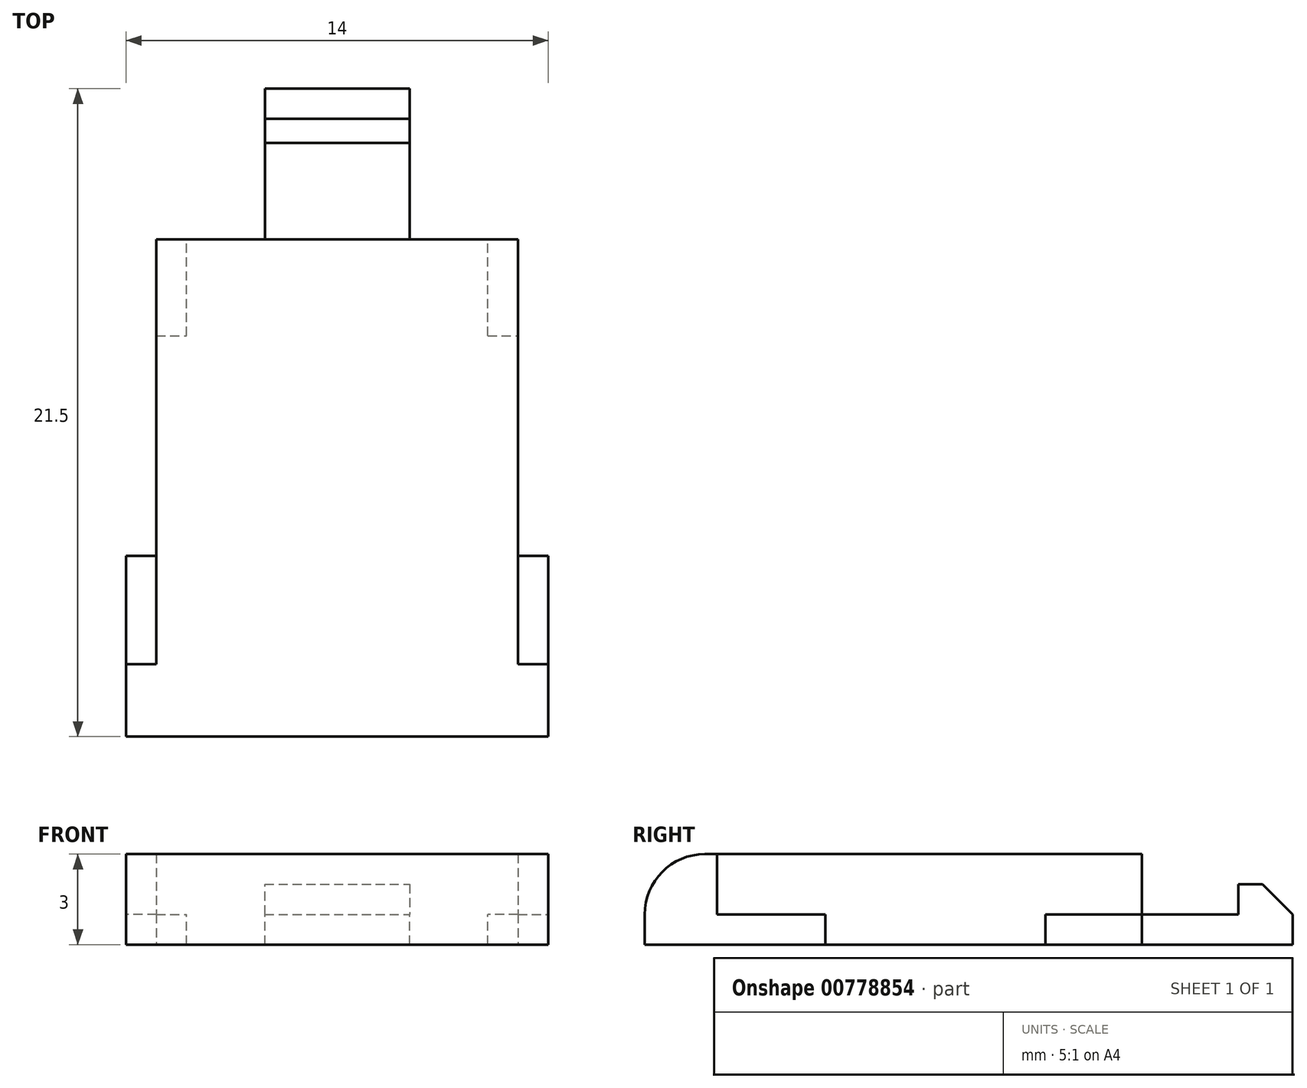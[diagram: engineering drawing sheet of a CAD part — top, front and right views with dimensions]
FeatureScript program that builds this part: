
annotation { "Feature Type Name" : "Feature", "Feature Type Description" : "" }
export const myFeature = defineFeature(function(context is Context, id is Id, definition is map)
    precondition{}
    {
        {
            var Q0;
            Q0=qCreatedBy(makeId("Front.planeOp"),FACE);
            var sketch = newSketch(context, id + "F0", { "sketchPlane" : qUnion([Q0])});
            skLineSegment(sketch, "E0.bottom", {"start": v(-6, 3) * mm, "end": v(6, 3) * mm});
            skLineSegment(sketch, "E0.top", {"start": v(-6, 0) * mm, "end": v(6, 0) * mm});
            skLineSegment(sketch, "E0.left", {"start": v(-6, 3) * mm, "end": v(-6, 0) * mm});
            skLineSegment(sketch, "E0.right", {"start": v(6, 3) * mm, "end": v(6, 0) * mm});
            skLineSegment(sketch, "E1", {"start": v(6, 1) * mm, "end": v(-6, 1) * mm});
            skLineSegment(sketch, "E2.bottom", {"start": v(6, 3) * mm, "end": v(7, 3) * mm});
            skLineSegment(sketch, "E2.top", {"start": v(6, 0) * mm, "end": v(7, 0) * mm});
            skLineSegment(sketch, "E2.right", {"start": v(7, 3) * mm, "end": v(7, 0) * mm});
            skLineSegment(sketch, "E3.bottom", {"start": v(-6, 3) * mm, "end": v(-7, 3) * mm});
            skLineSegment(sketch, "E3.top", {"start": v(-6, 0) * mm, "end": v(-7, 0) * mm});
            skLineSegment(sketch, "E3.right", {"start": v(-7, 3) * mm, "end": v(-7, 0) * mm});
            skLineSegment(sketch, "E4", {"start": v(-6, 1) * mm, "end": v(-7, 1) * mm});
            skLineSegment(sketch, "E5", {"start": v(6, 1) * mm, "end": v(7, 1) * mm});
            skPoint(sketch, "E6", {"position": v(0, 0) * mm});
            skSolve(sketch);
        }
        {
            var Q0;
            {var subQ0=sQuery(id+"F0.wireOp",EDGE,"E0.top");Q0=makeQuery(id+"F0.imprint","IMPRINT",FACE,{"disambiguationData":[TD([[makeQuery(id+"F0.imprint","IMPRINT",EDGE,{"derivedFrom":subQ0}),1.0]])]});}
            var Q1;
            {var subQ0=sQuery(id+"F0.wireOp",EDGE,"E0.bottom");Q1=makeQuery(id+"F0.imprint","IMPRINT",FACE,{"disambiguationData":[TD([[makeQuery(id+"F0.imprint","IMPRINT",EDGE,{"derivedFrom":subQ0}),-1.0]])]});}
            extrude(context, id + "F1", {"entities" : qUnion([Q0, Q1]), "oppositeDirection" : true, "depth" : 16.5 * mm, "offsetDistance" : 25 * mm});
        }
        {
            var Q0;
            {var subQ0=sQuery(id+"F0.wireOp",EDGE,"E3.bottom");Q0=makeQuery(id+"F0.imprint","IMPRINT",FACE,{"disambiguationData":[TD([[makeQuery(id+"F0.imprint","IMPRINT",EDGE,{"derivedFrom":subQ0}),1.0]])]});}
            var Q1;
            {var subQ0=sQuery(id+"F0.wireOp",EDGE,"E2.bottom");Q1=makeQuery(id+"F0.imprint","IMPRINT",FACE,{"disambiguationData":[TD([[makeQuery(id+"F0.imprint","IMPRINT",EDGE,{"derivedFrom":subQ0}),-1.0]])]});}
            extrude(context, id + "F2", {"entities" : qUnion([Q0, Q1]), "operationType" : NewBodyOperationType.ADD, "oppositeDirection" : true, "depth" : 2.4 * mm, "offsetDistance" : 25 * mm});
        }
        {
            var Q0;
            {var subQ0=sQuery(id+"F0.wireOp",EDGE,"E2.top");Q0=makeQuery(id+"F0.imprint","IMPRINT",FACE,{"disambiguationData":[TD([[makeQuery(id+"F0.imprint","IMPRINT",EDGE,{"derivedFrom":subQ0}),1.0]])]});}
            var Q1;
            {var subQ0=sQuery(id+"F0.wireOp",EDGE,"E3.top");Q1=makeQuery(id+"F0.imprint","IMPRINT",FACE,{"disambiguationData":[TD([[makeQuery(id+"F0.imprint","IMPRINT",EDGE,{"derivedFrom":subQ0}),-1.0]])]});}
            extrude(context, id + "F3", {"entities" : qUnion([Q0, Q1]), "operationType" : NewBodyOperationType.ADD, "oppositeDirection" : true, "depth" : 6 * mm, "offsetDistance" : 25 * mm});
        }
        {
            var Q0;
            Q0=makeQuery(id+"F2.boolean.opBoolean","MERGE",EDGE,{"derivedFrom":[makeQuery(id+"F1.opExtrude","CAP_EDGE",EDGE,{"disambiguationData":[OSD([sQuery(id+"F0.wireOp",EDGE,"E0.bottom")])],"isStart":true}),makeQuery(id+"F2.opExtrude","CAP_EDGE",EDGE,{"disambiguationData":[OSD([sQuery(id+"F0.wireOp",EDGE,"E2.bottom")])],"isStart":true}),makeQuery(id+"F2.opExtrude","CAP_EDGE",EDGE,{"disambiguationData":[OSD([sQuery(id+"F0.wireOp",EDGE,"E3.bottom")])],"isStart":true})]});
            fillet(context, id + "F4", {"entities" : qUnion([Q0]), "radius" : 2 * mm, "tangentPropagation" : true, "allowEdgeOverflow" : false});
        }
        {
            var Q0;
            Q0=makeQuery(id+"F1.opExtrude","CAP_FACE",FACE,{"disambiguationData":[OSD([sQuery(id+"F0.wireOp",EDGE,"E0.bottom"),sQuery(id+"F0.wireOp",EDGE,"E0.top"),sQuery(id+"F0.wireOp",EDGE,"E0.right"),sQuery(id+"F0.wireOp",EDGE,"E0.left")])],"isStart":false});
            var sketch = newSketch(context, id + "F5", { "sketchPlane" : qUnion([Q0])});
            skLineSegment(sketch, "E7.bottom", {"start": v(-6, 0) * mm, "end": v(-5, 0) * mm});
            skLineSegment(sketch, "E7.top", {"start": v(-6, 1) * mm, "end": v(-5, 1) * mm});
            skLineSegment(sketch, "E7.left", {"start": v(-6, 0) * mm, "end": v(-6, 1) * mm});
            skLineSegment(sketch, "E7.right", {"start": v(-5, 0) * mm, "end": v(-5, 1) * mm});
            skLineSegment(sketch, "E8.MirrorCS", {"start": v(6, 1) * mm, "end": v(5, 1) * mm});
            skLineSegment(sketch, "E9.MirrorCS", {"start": v(5, 0) * mm, "end": v(5, 1) * mm});
            skLineSegment(sketch, "E10.bottom", {"start": v(2.4, 0) * mm, "end": v(-2.4, 0) * mm});
            skLineSegment(sketch, "E10.top", {"start": v(2.4, 1) * mm, "end": v(-2.4, 1) * mm});
            skLineSegment(sketch, "E10.left", {"start": v(2.4, 0) * mm, "end": v(2.4, 1) * mm});
            skLineSegment(sketch, "E10.right", {"start": v(-2.4, 0) * mm, "end": v(-2.4, 1) * mm});
            skSolve(sketch);
        }
        {
            var Q0;
            {var subQ0=sQuery(id+"F5.wireOp",EDGE,"E8.MirrorCS");Q0=makeQuery(id+"F5.imprint","IMPRINT",FACE,{"disambiguationData":[TD([[makeQuery(id+"F5.imprint","IMPRINT",EDGE,{"derivedFrom":subQ0}),1.0]])]});}
            var Q1;
            Q1=makeQuery(id+"F5.imprint","IMPRINT",FACE,{"disambiguationData":[TD([[makeQuery(id+"F5.imprint","IMPRINT",EDGE,{"derivedFrom":sQuery(id+"F5.wireOp",EDGE,"E7.bottom")}),-1.0]])]});
            extrude(context, id + "F6", {"entities" : qUnion([Q0, Q1]), "operationType" : NewBodyOperationType.REMOVE, "oppositeDirection" : true, "depth" : 3.2 * mm, "offsetDistance" : 25 * mm});
        }
        {
            var Q0;
            Q0=makeQuery(id+"F5.imprint","IMPRINT",FACE,{"disambiguationData":[TD([[makeQuery(id+"F5.imprint","IMPRINT",EDGE,{"derivedFrom":sQuery(id+"F5.wireOp",EDGE,"E10.bottom")}),-1.0]])]});
            extrude(context, id + "F7", {"entities" : qUnion([Q0]), "operationType" : NewBodyOperationType.ADD, "depth" : 5 * mm, "offsetDistance" : 25 * mm});
        }
        {
            var Q0;
            Q0=makeQuery(id+"F7.opExtrude","SWEPT_FACE",FACE,{"disambiguationData":[OSD([sQuery(id+"F5.wireOp",EDGE,"E10.top")])]});
            var sketch = newSketch(context, id + "F8", { "sketchPlane" : qUnion([Q0])});
            skLineSegment(sketch, "E11.bottom", {"start": v(-2.4, 21.5) * mm, "end": v(2.4, 21.5) * mm});
            skLineSegment(sketch, "E11.top", {"start": v(-2.4, 19.7) * mm, "end": v(2.4, 19.7) * mm});
            skLineSegment(sketch, "E11.left", {"start": v(-2.4, 21.5) * mm, "end": v(-2.4, 19.7) * mm});
            skLineSegment(sketch, "E11.right", {"start": v(2.4, 21.5) * mm, "end": v(2.4, 19.7) * mm});
            skSolve(sketch);
        }
        {
            var Q0;
            Q0=makeQuery(id+"F8.imprint","IMPRINT",FACE,{"disambiguationData":[TD([[makeQuery(id+"F8.imprint","IMPRINT",EDGE,{"derivedFrom":sQuery(id+"F8.wireOp",EDGE,"E11.bottom")}),-1.0]])]});
            extrude(context, id + "F9", {"entities" : qUnion([Q0]), "operationType" : NewBodyOperationType.ADD, "depth" : 1 * mm, "offsetDistance" : 25 * mm});
        }
        {
            var Q0;
            Q0=makeQuery(id+"F9.opExtrude","CAP_EDGE",EDGE,{"disambiguationData":[OSD([sQuery(id+"F8.wireOp",EDGE,"E11.bottom")])],"isStart":false});
            chamfer(context, id + "F10", {"entities" : qUnion([Q0]), "width" : 1 * mm, "tangentPropagation" : true});
        }
    });
